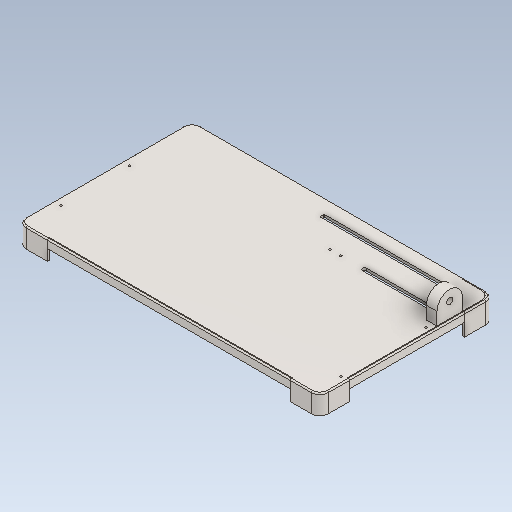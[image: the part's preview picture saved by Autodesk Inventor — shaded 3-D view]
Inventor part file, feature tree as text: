
AUTODESK INVENTOR PART (.ipt)
format: ipt  version: 2021 (Build 250183000, 183)  size: 184,320 bytes
history: mixed  units: mm
features: other x7, fillet x3, imported_body x1
ambient origin geometry x8: Origin, YZ Plane, XZ Plane, XY Plane, X Axis, Y Axis, Z Axis, Center Point
bodies: Body1 (imported_parasolid), Body2 (imported_parasolid), Body3 (imported_parasolid), Body4 (imported_parasolid), Body5 (imported_parasolid)
feature tree (11):
  other  "Sólido1"
  other  "Sólido2"
  other  "Sólido3"
  other  "Sólido4"
  other  "Sólido5"
  fillet  "Fillet3"  [1 undecoded]
  fillet  "Fillet4"  [1 undecoded]
  fillet  "Fillet6"  [1 undecoded]
  other  "Cut-Extrude3"
  other  "Ø5.0 (5) Diameter Hole3"
  imported_body  NMx_Import_Brep_tag  [imported B-rep: ~94 faces, bbox_mm=[710.0, 86.0, 410.0]]
note: 3 required parameter values undecoded (feature->parameter linkage not recoverable at this tier; creation-order binding heuristic only, values carry confidence <= 0.55)
